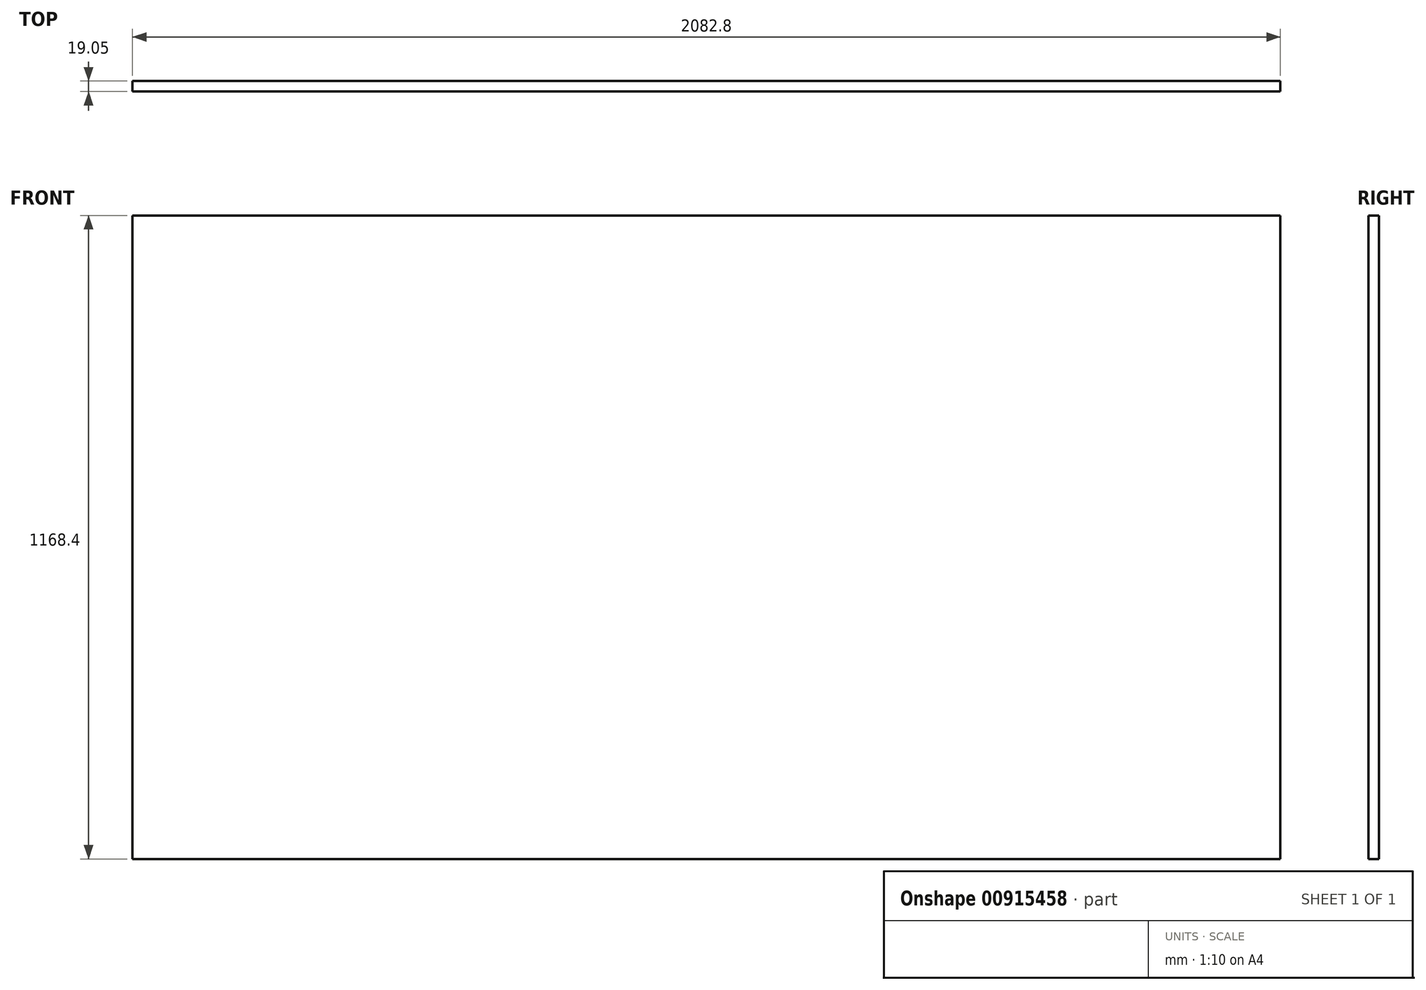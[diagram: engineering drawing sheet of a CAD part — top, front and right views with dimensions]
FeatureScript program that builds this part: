
annotation { "Feature Type Name" : "Feature", "Feature Type Description" : "" }
export const myFeature = defineFeature(function(context is Context, id is Id, definition is map)
    precondition{}
    {
        {
            var Q0;
            Q0=qCreatedBy(makeId("Front.planeOp"),FACE);
            var sketch = newSketch(context, id + "F0", { "sketchPlane" : qUnion([Q0])});
            skLineSegment(sketch, "E0.bottom", {"start": v(1041.4, 584.2) * mm, "end": v(-1041.4, 584.2) * mm});
            skLineSegment(sketch, "E0.top", {"start": v(1041.4, -584.2) * mm, "end": v(-1041.4, -584.2) * mm});
            skLineSegment(sketch, "E0.left", {"start": v(1041.4, 584.2) * mm, "end": v(1041.4, -584.2) * mm});
            skLineSegment(sketch, "E0.right", {"start": v(-1041.4, 584.2) * mm, "end": v(-1041.4, -584.2) * mm});
            skPoint(sketch, "E0.middle", {"position": v(0, 0) * mm});
            skSolve(sketch);
        }
        {
            var Q0;
            Q0=makeQuery(id+"F0.imprint","IMPRINT",FACE,{"disambiguationData":[TD([[makeQuery(id+"F0.imprint","IMPRINT",EDGE,{"derivedFrom":sQuery(id+"F0.wireOp",EDGE,"E0.bottom")}),1.0]])]});
            extrude(context, id + "F1", {"entities" : qUnion([Q0]), "depth" : 19.05 * mm, "offsetDistance" : 25.4 * mm});
        }
    });
